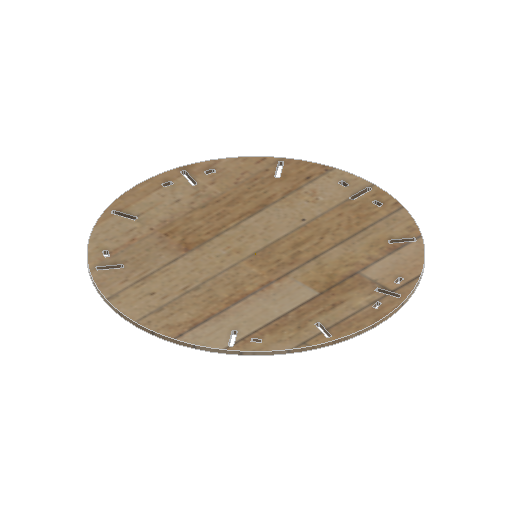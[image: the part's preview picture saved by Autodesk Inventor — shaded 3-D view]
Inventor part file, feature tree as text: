
AUTODESK INVENTOR PART (.ipt)
format: ipt  version: 2021 (Build 250183000, 183)  size: 436,224 bytes
history: native  units: mm
features: extrude x3, sketch x2
ambient origin geometry x8: Origin, YZ Plane, XZ Plane, XY Plane, X Axis, Y Axis, Z Axis, Center Point
bodies: Solid1 (feature_tree)
feature tree (5):
  sketch  "Sketch2"  dims[d4=30.0mm d5=3.25mm d9=400.0mm d10=6.0mm d11=0.0mm d12=8.0mm d13=0.0mm d14=6.5mm d20=18.666667mm d21=1.333333mm d22=1.333333mm d28=0.0mm d29=0.0mm d36=32.666667mm d37=3.25mm d38=13.083333mm d39=13.083333mm d43=10.0mm]
  sketch  "Sketch1"  dims[d2=6.5mm d3=1.333333mm]
  extrude  "Extrusion1"  Depth=1.333333mm
  extrude  "Extrusion2"  Depth=10.0mm
  extrude  "Extrusion3"  Depth=10.0mm
